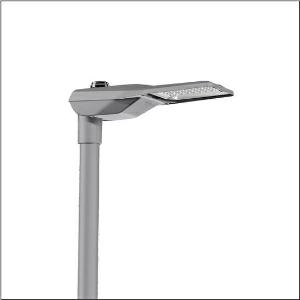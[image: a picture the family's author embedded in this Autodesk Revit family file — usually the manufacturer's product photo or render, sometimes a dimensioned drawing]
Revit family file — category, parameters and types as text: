
# Revit family: streetlight_sl_21_mini___st0_5a_5xe6b47n08gb_d394
name_source: partatom
category: Lighting Fixtures
units: mm (PartAtom-declared; Revit-internal decimal feet)

## family parameters
Cut with Voids When Loaded = No
Host = Face
Light Source = No
Part Type = Normal
Room Calculation Point = No
Round Connector Dimension = Use Diameter
Shared = No

## types (1)
- --- (1 x LED, 6180 lm, 40.4 W, 4000K)
    Apparent Load = 40 VA
    CIE Flux Codes = 41 75 97 100 100
    Color Rendering = 70
    Color Temperature = 4000K
    Default Elevation = 1800 mm
    Description = Streetlight SL 21 mini, mast luminaire, primary light control with lens, of PMMA, primary optical cover: cover, of toughened safety glass, transparent, light distribution: ST0.5a, light emission: direct distribution, primary light characteristic: asymmetric, installation type: side-entry, LED, 3G 1.5mm², High Power LED, rated luminous flux: 6.180lm, luminous efficacy: 153lm/W, light colour: 740, colour temperature: 4000K, control: overheat protection, presetting dimming linear, constant luminous flux control, time-dependent luminous flux control, flexible luminous flux parameterisation, mains connection: 230..240V, AC, 50/60Hz, connection cable pre-assembled, cable length: 8,5m, wiring characteristics: H07RN-F, start of lifetime: 40W, end of service life: 41W, reduction: 19W, luminaire housing, of diecast aluminium (EN AC-44300), powder-coated, Siteco® metallic grey (DB 702S), corrosivity category C5 mid according to DIN EN ISO 12944, multi-level sealing system, sealing non-destructively replaceable, inclination adjustable: 0°, 5°, 10°, 15°, length: 628mm, width: 235mm, height: 110mm, spigot size: 42mm (side-entry), protection rating (complete): IP66, insulation class (complete): insulation class I (protective earthing), certification: CE, ENEC, ENEC+, VDE, impact resistance: IK09, permissible operating ambient temperature for outdoor applications: -40..+50°C, standard-compliant lighting for roads and squares, packaging unit: 1 piece

Light Distribution: ST0.5a
    Height = 110 mm
    Lamp = 1 x LED
    Lamp Light Flux = 6180 lm
    Lamp Power = 40.4 W
    Lamp count = 1
    Length = 625 mm
    Luminous efficacy = 153 lm/W
    Manufacturer = Siteco
    ModVariant = No
    Model = 5XE6B47N08GB
    Number of Poles = 1
    OnlyDefault = Yes
    Power Factor = 1
    Product Name = Streetlight SL 21 mini | ST0.5a
    Product group = mast luminaire | pylon top
    ProductGroupID = 6100
    Protection Class = Protection class I
    Protection Degree = IP 66
    RLX_Detail_Level = 1
    RLX_Emergency_Light_Flux = 0 lm
    RLX_Emergency_Type = 0
    RLX_Emergency_Type_DB = No
    RlxData = <blob elided: 102737 chars, md5=b6a38edd>
    Socket = socket
    Standby Power = 0 W
    System Light Flux = 6180 lm
    System Power = 40 W
    Type Comments = factory setting: luminous flux: 100 % | dim-lin: 254 | 812 mA
    Type Image = l_1294379.jpg
    URL = http://relux.com
    VarID = @adj_068791
    Voltage = 0 V
    Weight = 0.00 kg
    Width = 234 mm

## geometry (parser evidence)
native form markers: Blend x4, Sweep x10
no freeform markers — native parametric forms only
